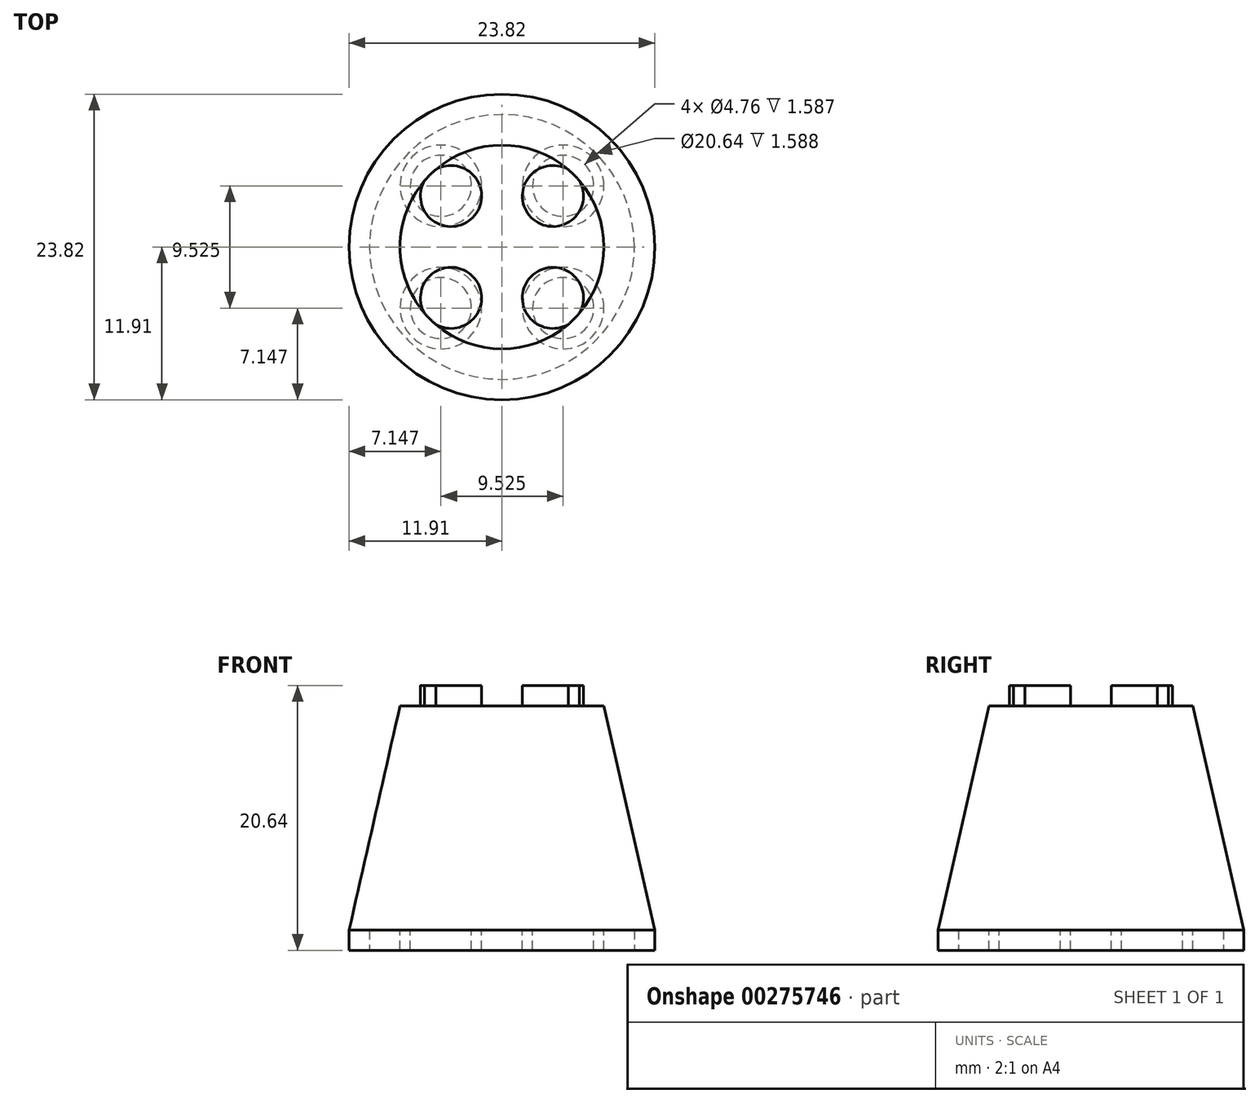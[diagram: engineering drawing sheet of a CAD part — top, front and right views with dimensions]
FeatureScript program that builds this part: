
annotation { "Feature Type Name" : "Feature", "Feature Type Description" : "" }
export const myFeature = defineFeature(function(context is Context, id is Id, definition is map)
    precondition{}
    {
        {
            var Q0;
            Q0=qCreatedBy(makeId("Front.planeOp"),FACE);
            var sketch = newSketch(context, id + "F0", { "sketchPlane" : qUnion([Q0])});
            skLineSegment(sketch, "E0", {"start": v(0, 0) * mm, "end": v(11.9, 0) * mm});
            skLineSegment(sketch, "E1", {"start": v(11.9, 0) * mm, "end": v(11.9, 1.59) * mm});
            skLineSegment(sketch, "E2", {"start": v(0, 0) * mm, "end": v(0, 1.59) * mm});
            skLineSegment(sketch, "E3", {"start": v(0, 1.59) * mm, "end": v(11.9, 1.59) * mm});
            skLineSegment(sketch, "E4", {"start": v(0, 0) * mm, "end": v(0, 19.05) * mm});
            skLineSegment(sketch, "E5", {"start": v(0, 19.05) * mm, "end": v(7.94, 19.05) * mm});
            skLineSegment(sketch, "E6", {"start": v(7.94, 19.05) * mm, "end": v(11.9, 1.59) * mm});
            skLineSegment(sketch, "E7", {"start": v(10.32, 0) * mm, "end": v(10.32, 1.59) * mm});
            skSolve(sketch);
        }
        {
            var Q0;
            {var subQ0=sQuery(id+"F0.wireOp",EDGE,"E1");Q0=makeQuery(id+"F0.imprint","IMPRINT",FACE,{"disambiguationData":[TD([[makeQuery(id+"F0.imprint","IMPRINT",EDGE,{"derivedFrom":subQ0}),1.0]])]});}
            var Q1;
            {var subQ0=sQuery(id+"F0.wireOp",EDGE,"E5");Q1=makeQuery(id+"F0.imprint","IMPRINT",FACE,{"disambiguationData":[TD([[makeQuery(id+"F0.imprint","IMPRINT",EDGE,{"derivedFrom":subQ0}),-1.0]])]});}
            var Q2;
            Q2=sQuery(id+"F0.wireOp",EDGE,"E4");
            revolve(context, id + "F1", {"entities" : qUnion([Q0, Q1]), "axis" : qUnion([Q2]), "revolveType" : RevolveType.FULL});
        }
        {
            var Q0;
            Q0=makeQuery(id+"F1.opRevolve","SWEPT_FACE",FACE,{"disambiguationData":[OSD([sQuery(id+"F0.wireOp",EDGE,"E5")])]});
            var sketch = newSketch(context, id + "F2", { "sketchPlane" : qUnion([Q0])});
            skLineSegment(sketch, "E8", {"start": v(0, 7.94) * mm, "end": v(0, -7.94) * mm});
            skLineSegment(sketch, "E9", {"start": v(-7.94, 0) * mm, "end": v(7.94, 0) * mm});
            skCircle(sketch, "E10", {"center": v(-3.97, -3.97) * mm, "radius": 2.38 * mm});
            skCircle(sketch, "E11.0.1.0", {"center": v(-3.97, 3.97) * mm, "radius": 2.38 * mm});
            skCircle(sketch, "E11.1.0.0", {"center": v(3.97, -3.97) * mm, "radius": 2.38 * mm});
            skCircle(sketch, "E11.1.1.0", {"center": v(3.97, 3.97) * mm, "radius": 2.38 * mm});
            skLineSegment(sketch, "E11.direction1", {"start": v(-3.97, -3.97) * mm, "end": v(3.97, -3.97) * mm, "construction": true});
            skLineSegment(sketch, "E11.direction2", {"start": v(-3.97, -3.97) * mm, "end": v(-3.97, 3.97) * mm, "construction": true});
            skSolve(sketch);
        }
        {
            var Q0;
            {var subQ0=sQuery(id+"F2.wireOp",EDGE,"E10");var subQ1=makeQuery(id+"F1.opRevolve","SWEPT_EDGE",EDGE,{"disambiguationData":[OSD([sQuery(id+"F0.wireOp",EDGE,"E5"),sQuery(id+"F0.wireOp",EDGE,"E6")])]});var subQ2=makeQuery(id+"F2.imprint","INTERSECT",VERTEX,{"disambiguationData":[OD(0.0)],"derivedFrom":[subQ1,subQ0]});Q0=makeQuery(id+"F2.imprint","IMPRINT",FACE,{"disambiguationData":[TD([[makeQuery(id+"F2.imprint","IMPRINT",EDGE,{"disambiguationData":[TD([[subQ2,-1.0]])],"derivedFrom":subQ0}),1.0]])]});}
            var Q1;
            {var subQ0=sQuery(id+"F2.wireOp",EDGE,"E11.0.1.0");var subQ1=makeQuery(id+"F1.opRevolve","SWEPT_EDGE",EDGE,{"disambiguationData":[OSD([sQuery(id+"F0.wireOp",EDGE,"E5"),sQuery(id+"F0.wireOp",EDGE,"E6")])]});var subQ2=makeQuery(id+"F2.imprint","INTERSECT",VERTEX,{"disambiguationData":[OD(0.0)],"derivedFrom":[subQ1,subQ0]});Q1=makeQuery(id+"F2.imprint","IMPRINT",FACE,{"disambiguationData":[TD([[makeQuery(id+"F2.imprint","IMPRINT",EDGE,{"disambiguationData":[TD([[subQ2,1.0]])],"derivedFrom":subQ0}),1.0]])]});}
            var Q2;
            {var subQ0=sQuery(id+"F2.wireOp",EDGE,"E11.1.1.0");var subQ1=makeQuery(id+"F1.opRevolve","SWEPT_EDGE",EDGE,{"disambiguationData":[OSD([sQuery(id+"F0.wireOp",EDGE,"E5"),sQuery(id+"F0.wireOp",EDGE,"E6")])]});var subQ2=makeQuery(id+"F2.imprint","INTERSECT",VERTEX,{"disambiguationData":[OD(0.0)],"derivedFrom":[subQ1,subQ0]});Q2=makeQuery(id+"F2.imprint","IMPRINT",FACE,{"disambiguationData":[TD([[makeQuery(id+"F2.imprint","IMPRINT",EDGE,{"disambiguationData":[TD([[subQ2,-1.0]])],"derivedFrom":subQ0}),1.0]])]});}
            var Q3;
            {var subQ0=sQuery(id+"F2.wireOp",EDGE,"E11.1.0.0");var subQ1=makeQuery(id+"F1.opRevolve","SWEPT_EDGE",EDGE,{"disambiguationData":[OSD([sQuery(id+"F0.wireOp",EDGE,"E5"),sQuery(id+"F0.wireOp",EDGE,"E6")])]});var subQ2=makeQuery(id+"F2.imprint","INTERSECT",VERTEX,{"disambiguationData":[OD(0.0)],"derivedFrom":[subQ1,subQ0]});Q3=makeQuery(id+"F2.imprint","IMPRINT",FACE,{"disambiguationData":[TD([[makeQuery(id+"F2.imprint","IMPRINT",EDGE,{"disambiguationData":[TD([[subQ2,1.0]])],"derivedFrom":subQ0}),1.0]])]});}
            extrude(context, id + "F3", {"entities" : qUnion([Q0, Q1, Q2, Q3]), "operationType" : NewBodyOperationType.ADD, "depth" : 1.59 * mm});
        }
        {
            var Q0;
            Q0=makeQuery(id+"F1.opRevolve","SWEPT_FACE",FACE,{"disambiguationData":[OSD([sQuery(id+"F0.wireOp",EDGE,"E3")])]});
            var sketch = newSketch(context, id + "F4", { "sketchPlane" : qUnion([Q0])});
            skLineSegment(sketch, "E12", {"start": v(0, 10.32) * mm, "end": v(0, -10.32) * mm});
            skLineSegment(sketch, "E13", {"start": v(-10.32, 0) * mm, "end": v(10.32, 0) * mm});
            skCircle(sketch, "E14", {"center": v(-4.76, -4.76) * mm, "radius": 3.18 * mm});
            skCircle(sketch, "E15.0", {"center": v(-4.76, -4.76) * mm, "radius": 2.38 * mm});
            skCircle(sketch, "E16.0.1.0", {"center": v(-4.76, 4.76) * mm, "radius": 3.18 * mm});
            skCircle(sketch, "E16.0.1.1", {"center": v(-4.76, 4.76) * mm, "radius": 2.38 * mm});
            skCircle(sketch, "E16.1.0.0", {"center": v(4.76, -4.76) * mm, "radius": 3.18 * mm});
            skCircle(sketch, "E16.1.0.1", {"center": v(4.76, -4.76) * mm, "radius": 2.38 * mm});
            skCircle(sketch, "E16.1.1.0", {"center": v(4.76, 4.76) * mm, "radius": 3.18 * mm});
            skCircle(sketch, "E16.1.1.1", {"center": v(4.76, 4.76) * mm, "radius": 2.38 * mm});
            skLineSegment(sketch, "E16.direction1", {"start": v(-4.76, -4.76) * mm, "end": v(4.76, -4.76) * mm, "construction": true});
            skLineSegment(sketch, "E16.direction2", {"start": v(-4.76, -4.76) * mm, "end": v(-4.76, 4.76) * mm, "construction": true});
            skSolve(sketch);
        }
        {
            var Q0;
            Q0=qSketchRegion(id+"F4",true);
            extrude(context, id + "F5", {"entities" : qUnion([Q0]), "operationType" : NewBodyOperationType.ADD, "depth" : 1.59 * mm});
        }
    });
